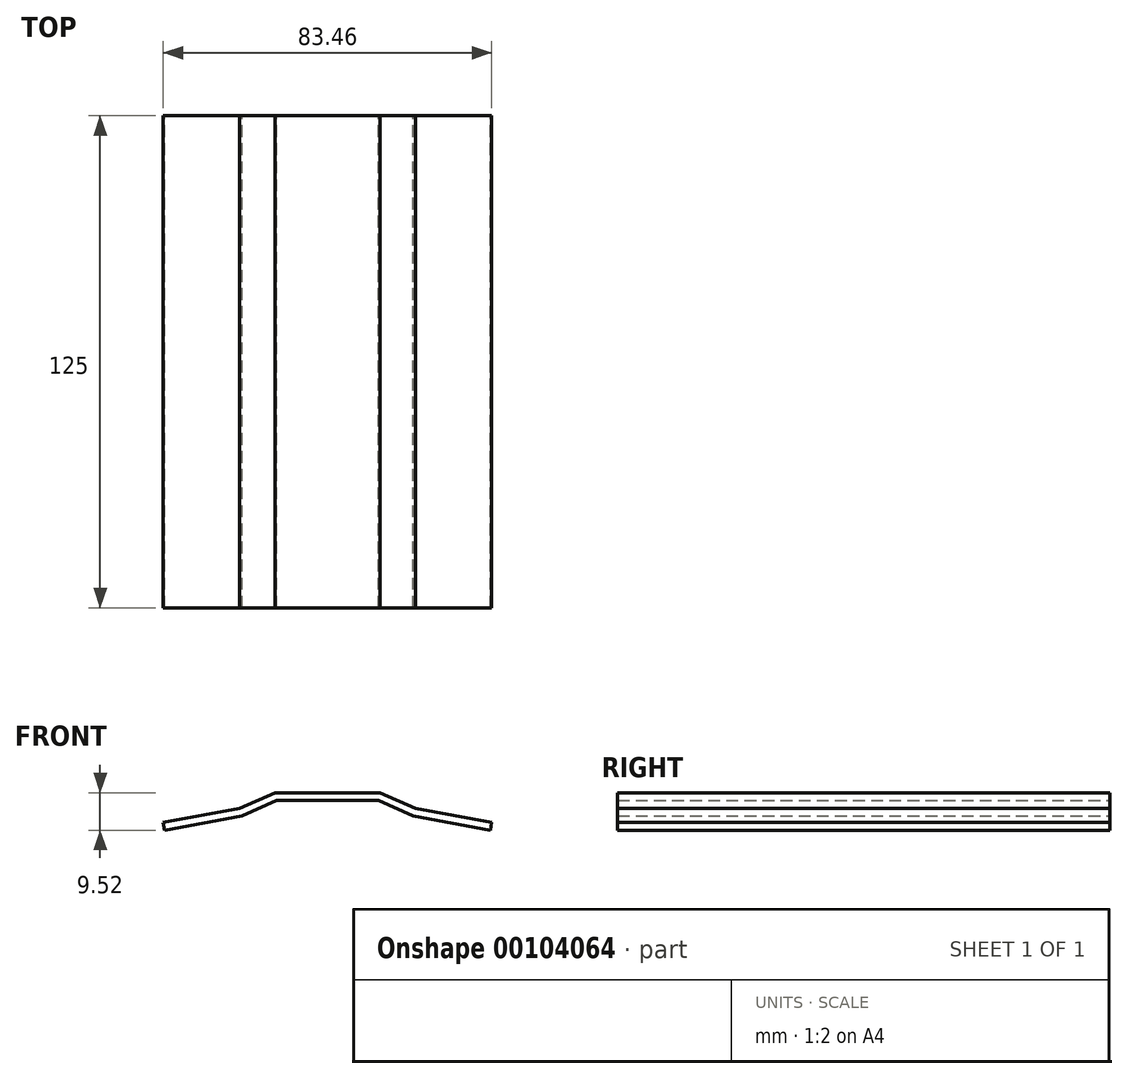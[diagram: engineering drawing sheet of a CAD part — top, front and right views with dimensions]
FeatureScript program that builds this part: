
annotation { "Feature Type Name" : "Feature", "Feature Type Description" : "" }
export const myFeature = defineFeature(function(context is Context, id is Id, definition is map)
    precondition{}
    {
        {
            var Q0;
            Q0=qCreatedBy(makeId("Front.planeOp"),FACE);
            var sketch = newSketch(context, id + "F0", { "sketchPlane" : qUnion([Q0])});
            skLineSegment(sketch, "E0", {"start": v(-41.36, 0) * mm, "end": v(-21.76, 3.63) * mm});
            skLineSegment(sketch, "E1", {"start": v(-21.76, 3.63) * mm, "end": v(-12.91, 7.52) * mm});
            skLineSegment(sketch, "E2", {"start": v(-12.91, 7.52) * mm, "end": v(0, 7.52) * mm});
            skLineSegment(sketch, "E3.MirrorCS", {"start": v(12.91, 7.52) * mm, "end": v(0, 7.52) * mm});
            skLineSegment(sketch, "E4.MirrorCS", {"start": v(21.76, 3.63) * mm, "end": v(12.91, 7.52) * mm});
            skLineSegment(sketch, "E5.MirrorCS", {"start": v(41.36, 0) * mm, "end": v(21.76, 3.63) * mm});
            skLineSegment(sketch, "E6.0", {"start": v(41.73, 1.97) * mm, "end": v(22.35, 5.56) * mm});
            skLineSegment(sketch, "E6.1", {"start": v(22.35, 5.56) * mm, "end": v(13.33, 9.52) * mm});
            skLineSegment(sketch, "E6.2", {"start": v(-41.73, 1.97) * mm, "end": v(-22.35, 5.56) * mm});
            skLineSegment(sketch, "E6.3", {"start": v(-22.35, 5.56) * mm, "end": v(-13.33, 9.52) * mm});
            skLineSegment(sketch, "E6.4", {"start": v(-13.33, 9.52) * mm, "end": v(0.02, 9.52) * mm});
            skLineSegment(sketch, "E6.5", {"start": v(13.33, 9.52) * mm, "end": v(0.02, 9.52) * mm});
            skLineSegment(sketch, "E7", {"start": v(-41.73, 1.97) * mm, "end": v(-41.36, 0) * mm});
            skLineSegment(sketch, "E8", {"start": v(41.73, 1.97) * mm, "end": v(41.36, 0) * mm});
            skSolve(sketch);
        }
        {
            var Q0;
            Q0 = qSketchRegion(id + "F0", true);
            extrude(context, id + "F1", {"entities" : qUnion([Q0]), "depth" : 125 * mm});
        }
    });
